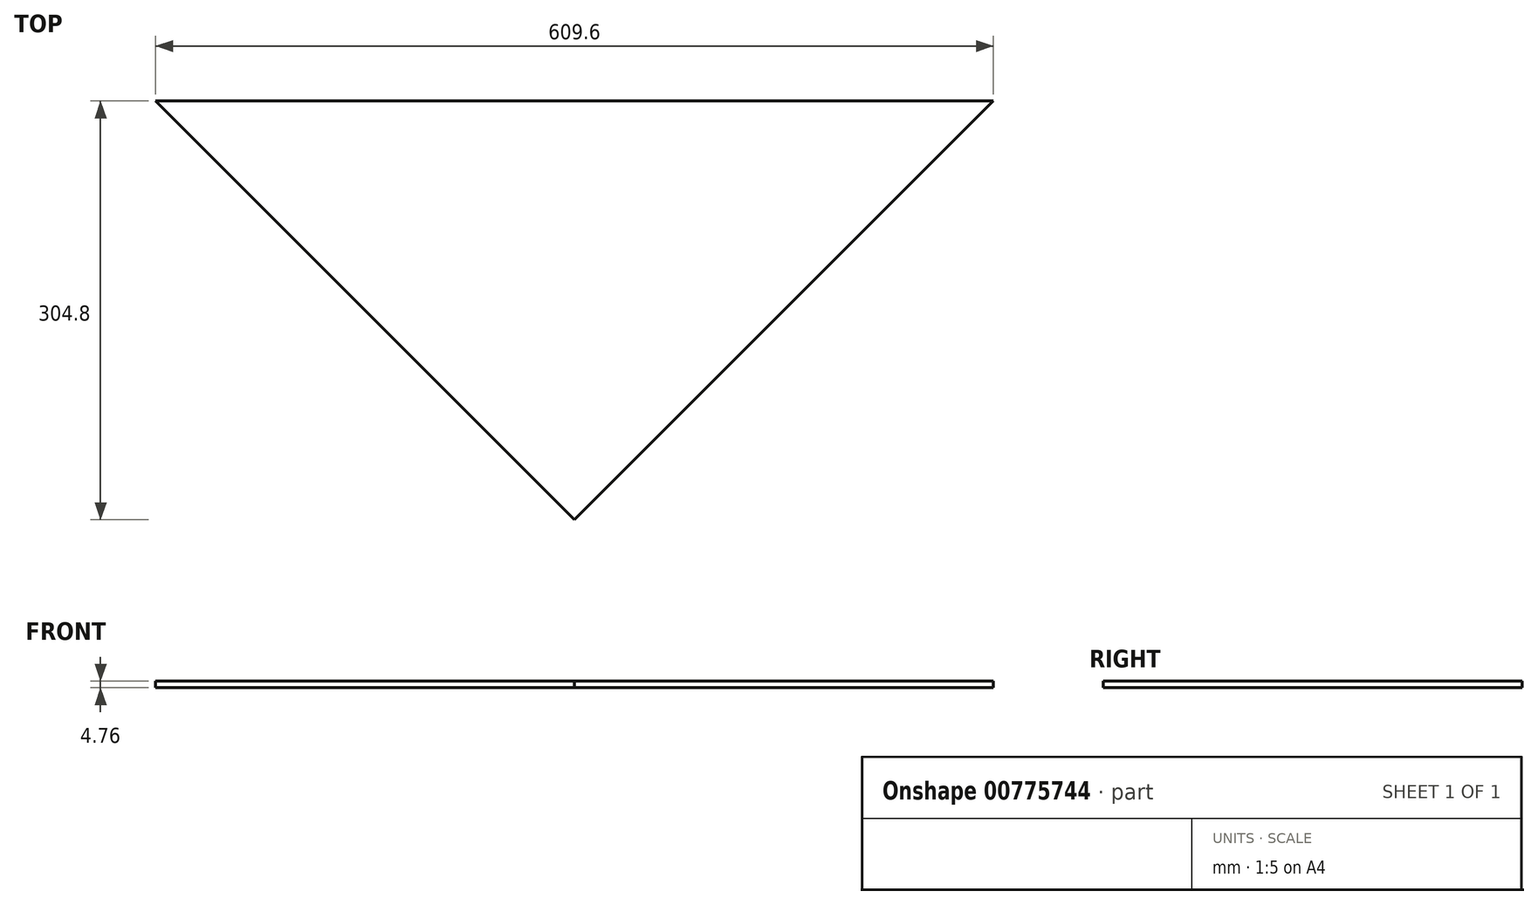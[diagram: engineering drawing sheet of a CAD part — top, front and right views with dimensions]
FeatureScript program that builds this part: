
annotation { "Feature Type Name" : "Feature", "Feature Type Description" : "" }
export const myFeature = defineFeature(function(context is Context, id is Id, definition is map)
    precondition{}
    {
        {
            var Q0;
            Q0=qCreatedBy(makeId("Top.planeOp"),FACE);
            var sketch = newSketch(context, id + "F0", { "sketchPlane" : qUnion([Q0])});
            skLineSegment(sketch, "E0", {"start": v(0, -304.8) * mm, "end": v(-304.8, 0) * mm});
            skLineSegment(sketch, "E1", {"start": v(0, -304.8) * mm, "end": v(304.8, 0) * mm});
            skLineSegment(sketch, "E2", {"start": v(304.8, 0) * mm, "end": v(-304.8, 0) * mm});
            skSolve(sketch);
        }
        {
            var Q0;
            Q0=makeQuery(id+"F0.imprint","IMPRINT",FACE,{"disambiguationData":[TD([[makeQuery(id+"F0.imprint","IMPRINT",EDGE,{"derivedFrom":sQuery(id+"F0.wireOp",EDGE,"E0")}),-1.0]])]});
            extrude(context, id + "F1", {"entities" : qUnion([Q0]), "endBound" : BoundingType.SYMMETRIC, "depth" : 4.76 * mm, "offsetDistance" : 25.4 * mm});
        }
    });
